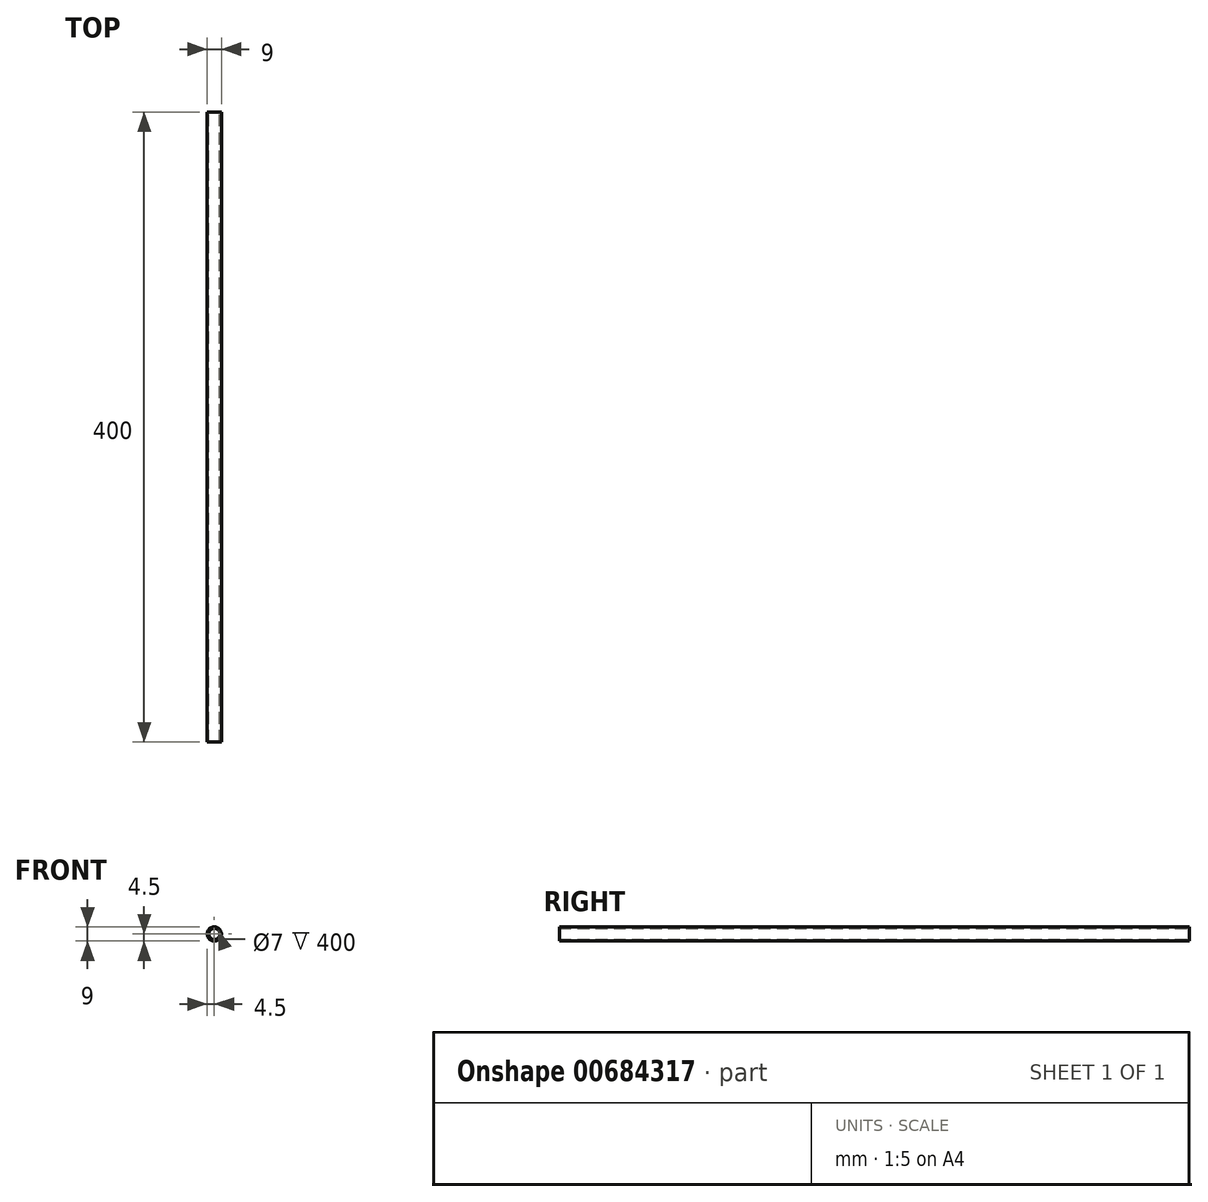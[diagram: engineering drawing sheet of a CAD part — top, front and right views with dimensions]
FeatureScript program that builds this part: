
annotation { "Feature Type Name" : "Feature", "Feature Type Description" : "" }
export const myFeature = defineFeature(function(context is Context, id is Id, definition is map)
    precondition{}
    {
        {
            var Q0;
            Q0=qCreatedBy(makeId("Front.planeOp"),FACE);
            var sketch = newSketch(context, id + "F0", { "sketchPlane" : qUnion([Q0])});
            skCircle(sketch, "E0", {"center": v(0, 0) * mm, "radius": 4.5 * mm});
            skCircle(sketch, "E1", {"center": v(0, 0) * mm, "radius": 3.5 * mm});
            skSolve(sketch);
        }
        {
            var Q0;
            Q0=makeQuery(id+"F0.imprint","IMPRINT",FACE,{"disambiguationData":[TD([[makeQuery(id+"F0.imprint","IMPRINT",EDGE,{"derivedFrom":sQuery(id+"F0.wireOp",EDGE,"E0")}),1.0]])]});
            extrude(context, id + "F1", {"entities" : qUnion([Q0]), "depth" : 400 * mm, "offsetDistance" : 25 * mm});
        }
    });
